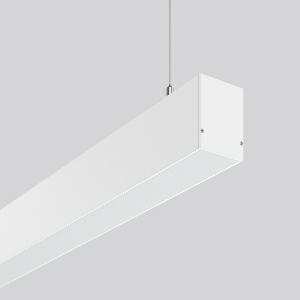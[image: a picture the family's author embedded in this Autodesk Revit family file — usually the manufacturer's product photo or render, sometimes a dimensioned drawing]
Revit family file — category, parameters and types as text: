
# Revit family: less_is_more_50_312312_002_1_5958
name_source: partatom
category: Lighting Fixtures
units: mm (PartAtom-declared; Revit-internal decimal feet)

## family parameters
Cut with Voids When Loaded = No
Host = Face
Light Source = No
Part Type = Normal
Room Calculation Point = No
Round Connector Dimension = Use Diameter
Shared = No

## types (1)
- LESS IS MORE 50 (1 x LED Modul 840, 3250 lm, 4000)
    Apparent Load = 28 VA
    CIE Flux Codes = 48 79 95 100 100
    Color Rendering = 80
    Color Temperature = 4000
    Default Elevation = 1800 mm
    Description = Series: LESS IS MORE 50
Linear pendant luminaire for aesthetically sophisticated lighting. Housing: extruded aluminium profile, powder-coated. End cap aluminium powder-coated. Canopy made of aluminium, powder-coated. Diffuser made of non-yellowing plastic (PMMA), opal. Direct light emission. Suitable for pendant. 2-point steel cable suspension freely positionable and infinitely height-adjustable. Special lengths available on request. LED unit with integrated converter interchangeable and removable. Suitable for through-wiring. With sensors or as a safety luminaire on request. 
Colour: traffic white, matt (RAL 9016)
Length: 1127 mm
Width: 57 mm
Height: 75 mm
Suspension length: 2000 mm
Lamp: LED
Socket: without socket
Colour temperature: 4000K
Colour rendering index (CRI): 80
System power: 28 W
Rated luminous flux: 3250 lm
Luminous efficiency: 116 lm/W
Control gear: Regulated power supply
Protection class: I
Type of protection: IP 20
    Height = 75 mm
    Lamp = 1 x LED Modul 840
    Lamp Light Flux = 3250 lm
    Lamp count = 1
    Length = 1127 mm
    Lifetime = 50000 h
    Luminous efficacy = 116 lm/W
    Manufacturer = RZB
    ModVariant = No
    Model = 312312.002.1
    Mounting Place = Ceiling
    Mounting Type = Pendant
    Number of Poles = 1
    OnlyDefault = Yes
    Power Factor = 1
    Product Name = LESS IS MORE 50
    Product group = Pendant LED linear luminaires
    ProductGroupID = 907
    Protection Class = Protection class I
    Protection Degree = IP 20
    RLX_Detail_Level = 1
    RLX_Emergency_Light_Flux = 0 lm
    RLX_Emergency_Type = 0
    RLX_Emergency_Type_DB = No
    RlxData = <blob elided: 20625 chars, md5=0f1bf33d>
    Socket = socket
    Standby Power = 0 W
    System Light Flux = 3250 lm
    System Power = 28 W
    Type Comments = Product without accessories
    Type Image = 312318.002.jpg
    URL = http://relux.com
    VarID = ---
    Voltage = 230 V
    Voltage Range = 220-240 V
    Weight = 0.00 kg
    Width = 57 mm

## geometry (parser evidence)
native form markers: Blend x4, Sweep x10
no freeform markers — native parametric forms only
